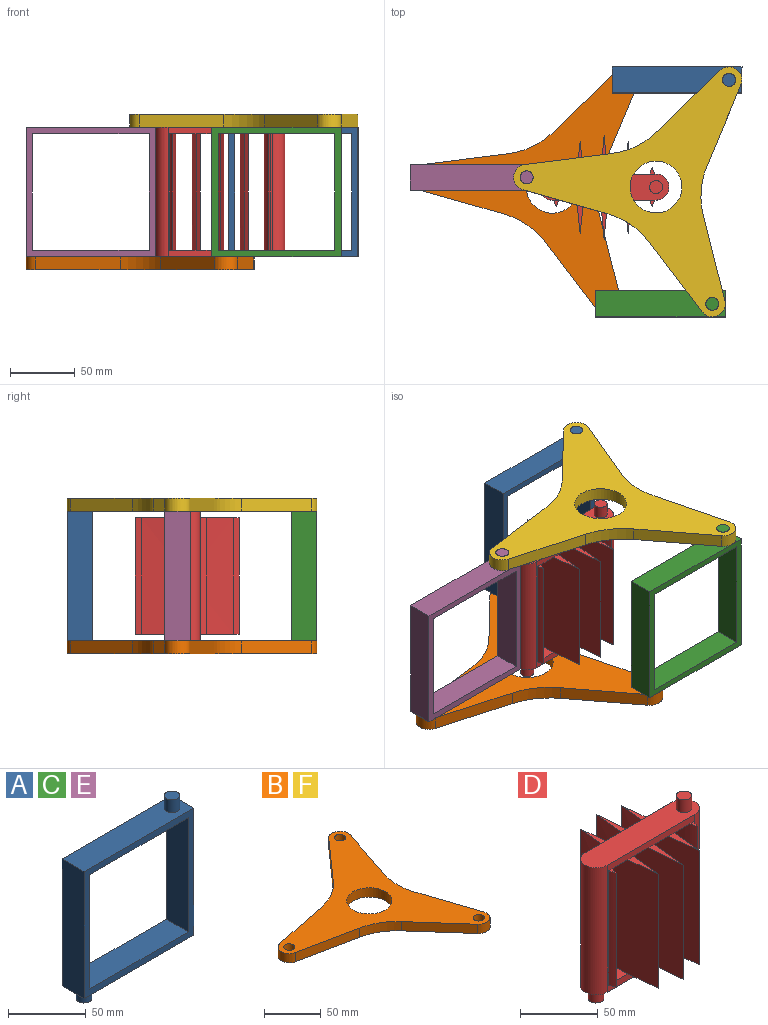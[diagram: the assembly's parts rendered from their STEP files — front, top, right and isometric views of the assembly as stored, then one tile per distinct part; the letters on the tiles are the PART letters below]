
ASSEMBLY  parts=6 mates=8
PART A: 14 faces, bbox 100x20x120 mm
  f0: plane 100x20mm, normal (0,0,1), area 1921.5mm2, adj f1,f7,f8,f9,f12
  f1: plane 100x20mm, normal (-1,0,0), area 2000mm2, adj f0,f2,f8,f9
  f2: plane 100x20mm, normal (0,0,-1), area 1921.5mm2, adj f1,f7,f8,f9,f10
  f3: plane 90x20mm, normal (0,0,-1), area 1800mm2, adj f4,f6,f8,f9
  f4: plane 90x20mm, normal (-1,0,0), area 1800mm2, adj f3,f5,f8,f9
  f5: plane 90x20mm, normal (0,0,1), area 1800mm2, adj f4,f6,f8,f9
  f6: plane 90x20mm, normal (1,0,0), area 1800mm2, adj f3,f5,f8,f9
  f7: plane 100x20mm, normal (1,0,0), area 2000mm2, adj f0,f2,f8,f9
  f8: plane 100x100mm, normal (0,-1,0), area 1900mm2, adj f0,f1,f2,f3,f4,f5,f6,f7
  f9: plane 100x100mm, normal (0,1,0), area 1900mm2, adj f0,f1,f2,f3,f4,f5,f6,f7
  f10: cylinder r=5mm len=10mm, axis (0,0,1), area 314.2mm2, adj f2,f11
  f11: plane 10x10mm, normal (0,0,-1), area 78.5mm2, adj f10
  f12: cylinder r=5mm len=10mm, axis (0,0,-1), area 314.2mm2, adj f0,f13
  f13: plane 10x10mm, normal (0,0,1), area 78.5mm2, adj f12
PART B: 18 faces, bbox 170x193.2x10 mm
  f0: plane 66.56x13.59mm, normal (-0.2,0.98,0), area 679.3mm2, adj f1,f13,f14,f15
  f1: cylinder r=10mm len=19.6mm, axis (0,0,-1), area 273.9mm2, adj f0,f2,f13,f14
  f2: plane 66.56x13.59mm, normal (-0.2,-0.98,0), area 679.3mm2, adj f1,f13,f14,f16
  f3: plane 50.85x45.05mm, normal (-0.75,-0.66,0), area 679.3mm2, adj f4,f13,f14,f16
  f4: cylinder r=10mm len=17.49mm, axis (0,0,-1), area 273.9mm2, adj f3,f5,f13,f14
  f5: plane 64.43x21.51mm, normal (0.95,0.32,0), area 679.3mm2, adj f4,f13,f14,f17
  f6: plane 64.43x21.51mm, normal (0.95,-0.32,0), area 679.3mm2, adj f7,f13,f14,f17
  f7: cylinder r=10mm len=17.49mm, axis (0,0,-1), area 273.9mm2, adj f6,f10,f13,f14
  f8: cylinder r=20mm len=40mm, axis (0,0,-1), area 1256.6mm2, adj f13,f14
  f9: cylinder r=5mm len=10mm, axis (0,0,-1), area 314.2mm2, adj f13,f14
  f10: plane 50.85x45.05mm, normal (-0.75,0.66,0), area 679.3mm2, adj f7,f13,f14,f15
  f11: cylinder r=5mm len=10mm, axis (0,0,-1), area 314.2mm2, adj f13,f14
  f12: cylinder r=5mm len=10mm, axis (0,0,-1), area 314.2mm2, adj f13,f14
  f13: plane 193.21x170mm, normal (0,0,1), area 9900.3mm2, adj f0,f1,f2,f3,f4,f5,f6,f7
  f14: plane 193.21x170mm, normal (0,0,-1), area 9900.3mm2, adj f0,f1,f2,f3,f4,f5,f6,f7
  f15: cylinder r=60mm len=32.91mm, axis (0,0,1), area 386.7mm2, adj f0,f10,f13,f14
  f16: cylinder r=60mm len=32.91mm, axis (0,0,1), area 386.7mm2, adj f2,f3,f13,f14
  f17: cylinder r=60mm len=38mm, axis (0,0,-1), area 386.7mm2, adj f5,f6,f13,f14
PART C: same geometry as A
PART D: 50 faces, bbox 100x80x120 mm
  f0: plane 20.03x13.11mm, normal (0,0,-1), area 254mm2, adj f6,f7,f40,f47
  f1: plane 20.03x13.11mm, normal (0,0,1), area 254mm2, adj f6,f7,f40,f47
  f2: plane 20.03x13.11mm, normal (0,0,-1), area 254mm2, adj f6,f7,f34,f41
  f3: plane 20.03x13.11mm, normal (0,0,1), area 254mm2, adj f6,f7,f34,f41
  f4: plane 20.03x14.11mm, normal (0,0,-1), area 260.6mm2, adj f6,f7,f24,f35
  f5: plane 20.03x14.11mm, normal (0,0,1), area 260.6mm2, adj f6,f7,f24,f35
  f6: plane 100x80mm, normal (0,-1,0), area 1028.6mm2, adj f0,f1,f2,f3,f4,f5,f8,f9
  f7: plane 100x80mm, normal (0,1,0), area 1028.6mm2, adj f0,f1,f2,f3,f4,f5,f8,f9
  f8: cylinder r=10mm len=100mm, axis (0,0,-1), area 3141.6mm2, adj f6,f7,f10,f11
  f9: cylinder r=10mm len=100mm, axis (0,0,-1), area 3141.6mm2, adj f6,f7,f10,f11
  f10: plane 100x20mm, normal (0,0,1), area 1835.6mm2, adj f6,f7,f8,f9,f12
  f11: plane 100x20mm, normal (0,0,-1), area 1835.6mm2, adj f6,f7,f8,f9,f14
  f12: cylinder r=5mm len=10mm, axis (0,0,-1), area 314.2mm2, adj f10,f13
  f13: plane 10x10mm, normal (0,0,1), area 78.5mm2, adj f12
  f14: cylinder r=5mm len=10mm, axis (0,0,1), area 314.2mm2, adj f11,f15
  f15: plane 10x10mm, normal (0,0,-1), area 78.5mm2, adj f14
  f16: plane 20.03x14.11mm, normal (0,0,-1), area 260.6mm2, adj f6,f7,f31,f46
  f17: plane 20.03x14.11mm, normal (0,0,1), area 260.6mm2, adj f6,f7,f31,f46
  f18: cylinder r=40mm len=90mm, axis (0,0,-1), area 493.5mm2, adj f6,f19,f21,f24
  f19: plane 5.2x3.46mm, normal (0,0,1), area 9.7mm2, adj f6,f18,f24
  f20: plane 5.2x3.46mm, normal (0,0,1), area 9.7mm2, adj f7,f23,f24
  f21: plane 5.2x3.46mm, normal (0,0,-1), area 9.7mm2, adj f6,f18,f24
  f22: plane 5.2x3.46mm, normal (0,0,-1), area 9.7mm2, adj f7,f23,f24
  f23: cylinder r=40mm len=90mm, axis (0,0,-1), area 493.5mm2, adj f7,f20,f22,f24
  f24: cylinder r=40mm len=90mm, axis (0,0,-1), area 2806.3mm2, adj f4,f5,f18,f19,f20,f21,f22,f23
  f25: cylinder r=40mm len=90mm, axis (0,0,-1), area 493.5mm2, adj f6,f26,f28,f31
  f26: plane 5.2x3.46mm, normal (0,0,1), area 9.7mm2, adj f6,f25,f31
  f27: plane 5.2x3.46mm, normal (0,0,1), area 9.7mm2, adj f7,f30,f31
  f28: plane 5.2x3.46mm, normal (0,0,-1), area 9.7mm2, adj f6,f25,f31
  f29: plane 5.2x3.46mm, normal (0,0,-1), area 9.7mm2, adj f7,f30,f31
  f30: cylinder r=40mm len=90mm, axis (0,0,-1), area 493.5mm2, adj f7,f27,f29,f31
  f31: cylinder r=40mm len=90mm, axis (0,0,-1), area 2806.3mm2, adj f16,f17,f25,f26,f27,f28,f29,f30
  f32: plane 25.52x5.47mm, normal (0,0,1), area 75.2mm2, adj f6,f34,f35
  f33: plane 25.52x5.47mm, normal (0,0,-1), area 75.2mm2, adj f6,f34,f35
  f34: extruded ~90x70.93mm, area 6411mm2, adj f2,f3,f32,f33,f35,f36,f37
  f35: extruded ~90x70.93mm, area 6411mm2, adj f4,f5,f32,f33,f34,f36,f37
  f36: plane 25.52x5.47mm, normal (0,0,1), area 75.2mm2, adj f7,f34,f35
  f37: plane 25.52x5.47mm, normal (0,0,-1), area 75.2mm2, adj f7,f34,f35
  f38: plane 30.07x5.62mm, normal (0,0,1), area 91.8mm2, adj f6,f40,f41
  f39: plane 30.07x5.62mm, normal (0,0,-1), area 91.8mm2, adj f6,f40,f41
  f40: extruded ~90x80mm, area 7224.2mm2, adj f0,f1,f38,f39,f41,f42,f43
  f41: extruded ~90x80mm, area 7224.2mm2, adj f2,f3,f38,f39,f40,f42,f43
  f42: plane 30.07x5.62mm, normal (0,0,1), area 91.8mm2, adj f7,f40,f41
  f43: plane 30.07x5.62mm, normal (0,0,-1), area 91.8mm2, adj f7,f40,f41
  f44: plane 25.52x5.47mm, normal (0,0,1), area 75.2mm2, adj f6,f46,f47
  f45: plane 25.52x5.47mm, normal (0,0,-1), area 75.2mm2, adj f6,f46,f47
  f46: extruded ~90x70.93mm, area 6411mm2, adj f16,f17,f44,f45,f47,f48,f49
  f47: extruded ~90x70.93mm, area 6411mm2, adj f0,f1,f44,f45,f46,f48,f49
  f48: plane 25.52x5.47mm, normal (0,0,1), area 75.2mm2, adj f7,f46,f47
  f49: plane 25.52x5.47mm, normal (0,0,-1), area 75.2mm2, adj f7,f46,f47
PART E: same geometry as A
PART F: same geometry as B
PLACE A t=(96.32,82.63,50)mm
PLACE B rot(axis=(0,0,-1),4.3deg) t=(0,0,-10)mm
PLACE C t=(83.4,-90.09,50)mm
PLACE D at identity fixed
PLACE E t=(-59.72,7.46,50)mm
PLACE F rot(axis=(0,0,-1),4.3deg) t=(80,0,100)mm
MATE revolute A.f12 <-> F.f7  axis (0,0,1) through (136.32,82.63,110)mm
MATE parallel A.f8 <-> C.f9  axis (0,-1,0) through (96.32,72.63,50)mm
MATE revolute B.f8 <-> D.f14  axis (0,0,-1) through (0,0,-10)mm
MATE revolute C.f10 <-> B.f4  axis (0,0,-1) through (43.4,-90.09,-10)mm
MATE revolute E.f10 <-> B.f11  axis (0,0,-1) through (-99.72,7.46,-10)mm
MATE revolute C.f12 <-> F.f4  axis (0,0,1) through (123.4,-90.09,110)mm
MATE revolute E.f12 <-> F.f11  axis (0,0,1) through (-19.72,7.46,110)mm
MATE revolute F.f8 <-> D.f12  axis (0,0,1) through (80,0,110)mm
